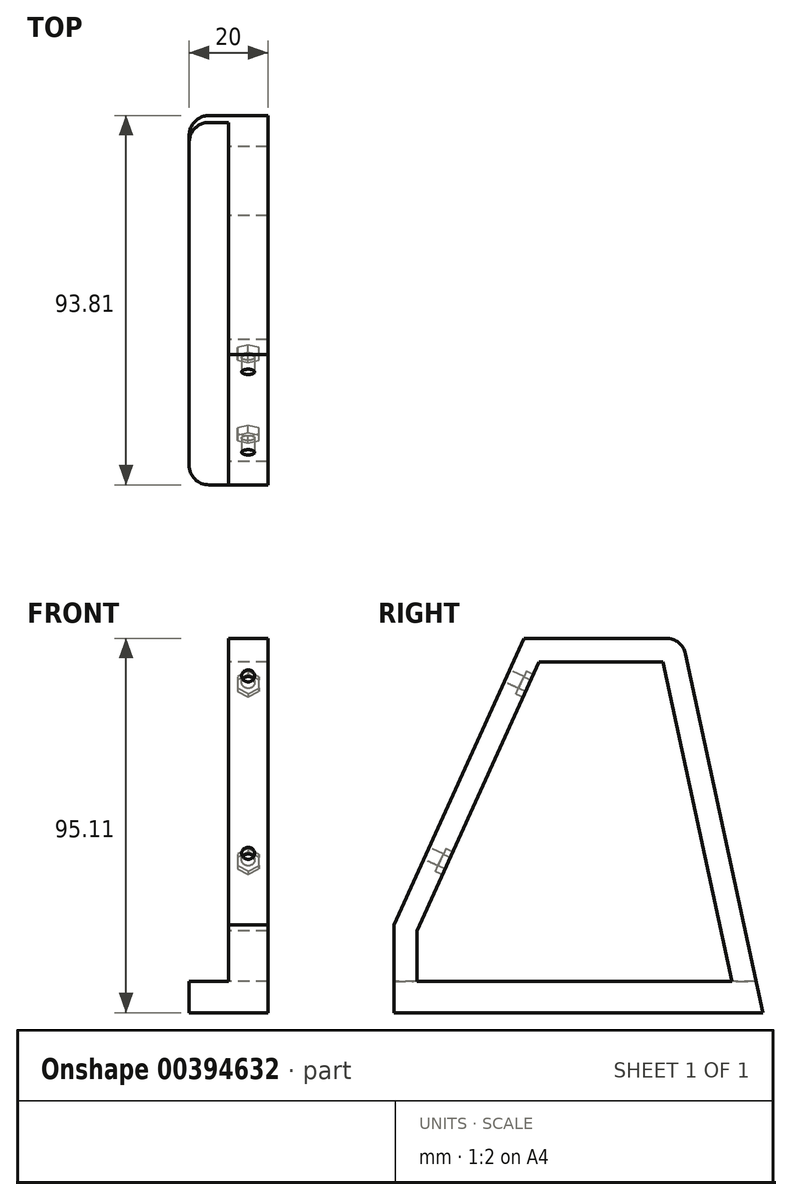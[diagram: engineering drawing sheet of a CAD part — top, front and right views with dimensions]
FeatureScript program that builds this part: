
annotation { "Feature Type Name" : "Feature", "Feature Type Description" : "" }
export const myFeature = defineFeature(function(context is Context, id is Id, definition is map)
    precondition{}
    {
        {
            var Q0;
            Q0=qCreatedBy(makeId("Right.planeOp"),FACE);
            var sketch = newSketch(context, id + "F0", { "sketchPlane" : qUnion([Q0])});
            skLineSegment(sketch, "E0", {"start": v(0, 0) * mm, "end": v(0, 22.26) * mm});
            skLineSegment(sketch, "E1", {"start": v(0, 22.26) * mm, "end": v(33.05, 95.11) * mm});
            skLineSegment(sketch, "E2", {"start": v(33.05, 95.11) * mm, "end": v(73.25, 95.11) * mm});
            skLineSegment(sketch, "E3", {"start": v(73.25, 95.11) * mm, "end": v(93.8, 0) * mm});
            skLineSegment(sketch, "E4", {"start": v(93.8, 0) * mm, "end": v(0, 0) * mm});
            skLineSegment(sketch, "E5", {"start": v(85.94, 8) * mm, "end": v(5.93, 8) * mm});
            skLineSegment(sketch, "E6", {"start": v(5.93, 8) * mm, "end": v(5.93, 20.81) * mm});
            skLineSegment(sketch, "E7", {"start": v(5.93, 20.81) * mm, "end": v(36.91, 89.11) * mm});
            skLineSegment(sketch, "E8", {"start": v(36.91, 89.11) * mm, "end": v(68.41, 89.11) * mm});
            skLineSegment(sketch, "E9", {"start": v(68.41, 89.11) * mm, "end": v(85.94, 8) * mm});
            skSolve(sketch);
        }
        {
            var Q0;
            Q0=makeQuery(id+"F0.imprint","IMPRINT",FACE,{"disambiguationData":[TD([[makeQuery(id+"F0.imprint","IMPRINT",EDGE,{"derivedFrom":sQuery(id+"F0.wireOp",EDGE,"E0")}),-1.0]])]});
            extrude(context, id + "F1", {"entities" : qUnion([Q0]), "depth" : 10 * mm, "offsetDistance" : 25 * mm});
        }
        {
            var Q0;
            Q0=makeQuery(id+"F1.opExtrude","CAP_FACE",FACE,{"disambiguationData":[OSD([sQuery(id+"F0.wireOp",EDGE,"E0"),sQuery(id+"F0.wireOp",EDGE,"E1"),sQuery(id+"F0.wireOp",EDGE,"E2"),sQuery(id+"F0.wireOp",EDGE,"E3"),sQuery(id+"F0.wireOp",EDGE,"E4"),sQuery(id+"F0.wireOp",EDGE,"E5"),sQuery(id+"F0.wireOp",EDGE,"E6"),sQuery(id+"F0.wireOp",EDGE,"E7"),sQuery(id+"F0.wireOp",EDGE,"E8"),sQuery(id+"F0.wireOp",EDGE,"E9")])],"isStart":true});
            var sketch = newSketch(context, id + "F2", { "sketchPlane" : qUnion([Q0])});
            skLineSegment(sketch, "E10", {"start": v(-92.08, 8) * mm, "end": v(0, 8) * mm});
            skSolve(sketch);
        }
        {
            var Q0;
            {var subQ4=makeQuery(id+"F1.opExtrude","CAP_EDGE",EDGE,{"disambiguationData":[OSD([sQuery(id+"F0.wireOp",EDGE,"E4")])],"isStart":true});Q0=makeQuery(id+"F2.imprint","IMPRINT",FACE,{"disambiguationData":[TD([[makeQuery(id+"F2.imprint","IMPRINT",EDGE,{"derivedFrom":subQ4}),1.0]])]});}
            extrude(context, id + "F3", {"entities" : qUnion([Q0]), "operationType" : NewBodyOperationType.ADD, "depth" : 10 * mm, "offsetDistance" : 25 * mm});
        }
        {
            var Q0;
            Q0=makeQuery(id+"F3.opExtrude","CAP_EDGE",EDGE,{"disambiguationData":[OSD([sQuery(id+"F0.wireOp",EDGE,"E3")])],"isStart":false});
            var Q1;
            Q1=makeQuery(id+"F3.opExtrude","CAP_EDGE",EDGE,{"disambiguationData":[OSD([sQuery(id+"F0.wireOp",EDGE,"E0")])],"isStart":false});
            var Q2;
            Q2=makeQuery(id+"F1.opExtrude","SWEPT_EDGE",EDGE,{"disambiguationData":[OSD([sQuery(id+"F0.wireOp",EDGE,"E2"),sQuery(id+"F0.wireOp",EDGE,"E3")])]});
            fillet(context, id + "F4", {"entities" : qUnion([Q0, Q1, Q2]), "radius" : 5 * mm, "tangentPropagation" : true, "allowEdgeOverflow" : false});
        }
        {
            var Q0;
            Q0=makeQuery(id+"F1.opExtrude","SWEPT_FACE",FACE,{"disambiguationData":[OSD([sQuery(id+"F0.wireOp",EDGE,"E1")])]});
            var sketch = newSketch(context, id + "F5", { "sketchPlane" : qUnion([Q0])});
            skPoint(sketch, "E11", {"position": v(5, 89.77) * mm});
            skPoint(sketch, "E11.positionSnap0", {"position": v(5, 100.27) * mm});
            skPoint(sketch, "E12", {"position": v(5, 40.27) * mm});
            skPoint(sketch, "E12.positionSnap0", {"position": v(5, 20.27) * mm});
            skSolve(sketch);
        }
        {
            var Q0;
            Q0=sQuery(id+"F5.wireOp",VERTEX,"E11");
            var Q1;
            Q1=sQuery(id+"F5.wireOp",VERTEX,"E12");
            var Q2;
            Q2=makeQuery(id+"F1.opExtrude","SWEPT_BODY",BODY,{"disambiguationData":[OSD([sQuery(id+"F0.wireOp",EDGE,"E0"),sQuery(id+"F0.wireOp",EDGE,"E1"),sQuery(id+"F0.wireOp",EDGE,"E2"),sQuery(id+"F0.wireOp",EDGE,"E3"),sQuery(id+"F0.wireOp",EDGE,"E4"),sQuery(id+"F0.wireOp",EDGE,"E5"),sQuery(id+"F0.wireOp",EDGE,"E6"),sQuery(id+"F0.wireOp",EDGE,"E7"),sQuery(id+"F0.wireOp",EDGE,"E8"),sQuery(id+"F0.wireOp",EDGE,"E9")])]});
            hole(context, id + "F6", {"style" : HoleStyle.SIMPLE, "endStyle" : HoleEndStyle.BLIND, "standardTappedOrClearance" : lookupTablePath({ "standard" : "ISO", "fit" : "Normal", "size" : "M3", "type" : "Clearance" }), "standardBlindInLast" : lookupTablePath({ "fit" : "Standard", "standard" : "ISO", "size" : "M3", "type" : "Clearance" }), "holeDiameter" : 3.3 * mm, "majorDiameter" : 5 * mm, "holeDepth" : 10 * mm, "isTappedThrough" : true, "tappedDepth" : 12 * mm, "tapClearance" : 3, "locations" : qUnion([Q0, Q1]), "scope" : qUnion([Q2])});
        }
        {
            var Q0;
            Q0=makeQuery(id+"F1.opExtrude","SWEPT_FACE",FACE,{"disambiguationData":[OSD([sQuery(id+"F0.wireOp",EDGE,"E7")])]});
            var sketch = newSketch(context, id + "F7", { "sketchPlane" : qUnion([Q0])});
            skCircle(sketch, "E13.cCircle", {"center": v(-5, 40.27) * mm, "radius": 2.75 * mm, "construction": true});
            skLineSegment(sketch, "E13.0", {"start": v(-7.75, 38.68) * mm, "end": v(-7.75, 41.86) * mm});
            skLineSegment(sketch, "E13.1", {"start": v(-7.75, 41.86) * mm, "end": v(-5, 43.45) * mm});
            skLineSegment(sketch, "E13.2", {"start": v(-5, 43.45) * mm, "end": v(-2.25, 41.86) * mm});
            skLineSegment(sketch, "E13.3", {"start": v(-2.25, 41.86) * mm, "end": v(-2.25, 38.68) * mm});
            skLineSegment(sketch, "E13.4", {"start": v(-2.25, 38.68) * mm, "end": v(-5, 37.1) * mm});
            skLineSegment(sketch, "E13.5", {"start": v(-5, 37.1) * mm, "end": v(-7.75, 38.68) * mm});
            skPoint(sketch, "E13.0.midPoint", {"position": v(-7.75, 40.27) * mm});
            skCircle(sketch, "E14.cCircle", {"center": v(-5, 89.77) * mm, "radius": 2.75 * mm, "construction": true});
            skLineSegment(sketch, "E14.0", {"start": v(-7.75, 88.18) * mm, "end": v(-7.75, 91.36) * mm});
            skLineSegment(sketch, "E14.1", {"start": v(-7.75, 91.36) * mm, "end": v(-5, 92.95) * mm});
            skLineSegment(sketch, "E14.2", {"start": v(-5, 92.95) * mm, "end": v(-2.25, 91.36) * mm});
            skLineSegment(sketch, "E14.3", {"start": v(-2.25, 91.36) * mm, "end": v(-2.25, 88.18) * mm});
            skLineSegment(sketch, "E14.4", {"start": v(-2.25, 88.18) * mm, "end": v(-5, 86.6) * mm});
            skLineSegment(sketch, "E14.5", {"start": v(-5, 86.6) * mm, "end": v(-7.75, 88.18) * mm});
            skPoint(sketch, "E14.0.midPoint", {"position": v(-7.75, 89.77) * mm});
            skSolve(sketch);
        }
        {
            var Q0;
            Q0 = qSketchRegion(id + "F7", true);
            extrude(context, id + "F8", {"entities" : qUnion([Q0]), "operationType" : NewBodyOperationType.REMOVE, "oppositeDirection" : true, "depth" : 2 * mm, "offsetDistance" : 25 * mm});
        }
    });
